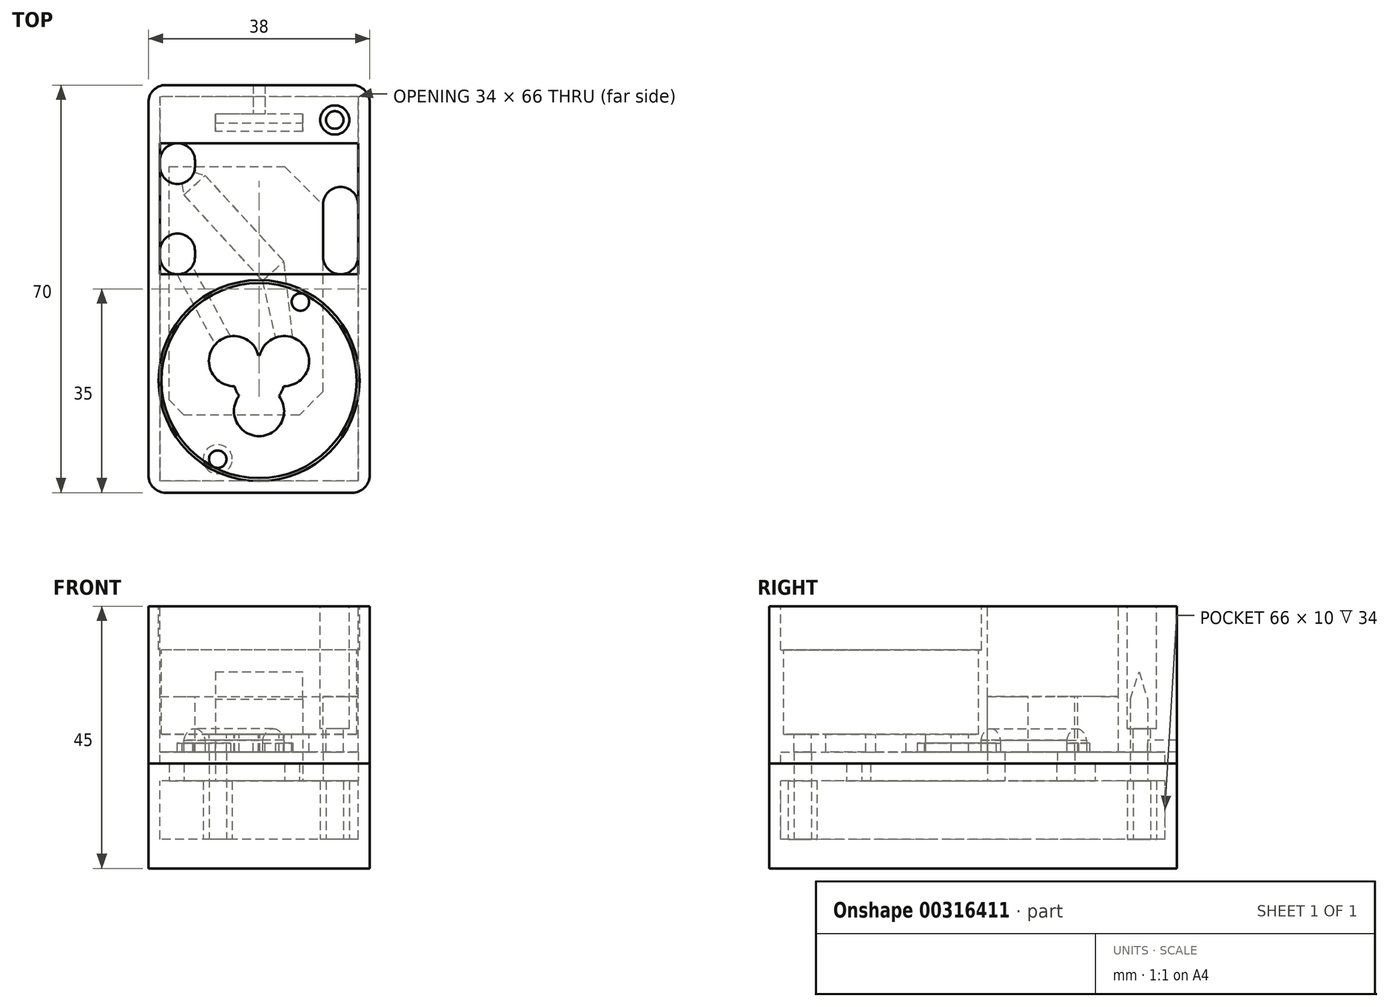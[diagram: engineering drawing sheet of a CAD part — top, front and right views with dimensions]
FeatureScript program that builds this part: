
annotation { "Feature Type Name" : "Feature", "Feature Type Description" : "" }
export const myFeature = defineFeature(function(context is Context, id is Id, definition is map)
    precondition{}
    {
        {
            var Q0;
            Q0=qCreatedBy(makeId("Top.planeOp"),FACE);
            var sketch = newSketch(context, id + "F0", { "sketchPlane" : qUnion([Q0])});
            skLineSegment(sketch, "E0.bottom", {"start": v(-16, 35) * mm, "end": v(16, 35) * mm});
            skLineSegment(sketch, "E0.top", {"start": v(-16, -35) * mm, "end": v(16, -35) * mm});
            skLineSegment(sketch, "E0.left", {"start": v(-19, 32) * mm, "end": v(-19, -32) * mm});
            skLineSegment(sketch, "E0.right", {"start": v(19, 32) * mm, "end": v(19, -32) * mm});
            skPoint(sketch, "E1.visualSharp", {"position": v(-19, 35) * mm});
            skArc(sketch, "E1.filletArc", {"start": v(-16, 35) * mm, "mid": v(-18.12, 34.12) * mm, "end": v(-19, 32) * mm});
            skPoint(sketch, "E2.visualSharp", {"position": v(-19, -35) * mm});
            skArc(sketch, "E2.filletArc", {"start": v(-19, -32) * mm, "mid": v(-18.12, -34.12) * mm, "end": v(-16, -35) * mm});
            skPoint(sketch, "E3.visualSharp", {"position": v(19, -35) * mm});
            skArc(sketch, "E3.filletArc", {"start": v(16, -35) * mm, "mid": v(18.12, -34.12) * mm, "end": v(19, -32) * mm});
            skPoint(sketch, "E4.visualSharp", {"position": v(19, 35) * mm});
            skArc(sketch, "E4.filletArc", {"start": v(19, 32) * mm, "mid": v(18.12, 34.12) * mm, "end": v(16, 35) * mm});
            skSolve(sketch);
        }
        {
            var Q0;
            Q0 = qSketchRegion(id + "F0", true);
            extrude(context, id + "F1", {"entities" : qUnion([Q0]), "depth" : 27 * mm});
        }
        {
            var Q0;
            Q0=makeQuery(id+"F1.opExtrude","CAP_FACE",FACE,{"disambiguationData":[OSD([sQuery(id+"F0.wireOp",EDGE,"E0.bottom"),sQuery(id+"F0.wireOp",EDGE,"E0.top"),sQuery(id+"F0.wireOp",EDGE,"E0.left"),sQuery(id+"F0.wireOp",EDGE,"E0.right"),sQuery(id+"F0.wireOp",EDGE,"E1.filletArc"),sQuery(id+"F0.wireOp",EDGE,"E2.filletArc"),sQuery(id+"F0.wireOp",EDGE,"E3.filletArc"),sQuery(id+"F0.wireOp",EDGE,"E4.filletArc")])],"isStart":false});
            var sketch = newSketch(context, id + "F2", { "sketchPlane" : qUnion([Q0])});
            skCircle(sketch, "E5", {"center": v(13, 29) * mm, "radius": 2.5 * mm});
            skSolve(sketch);
        }
        {
            var Q0;
            Q0 = qSketchRegion(id + "F2", true);
            extrude(context, id + "F3", {"entities" : qUnion([Q0]), "operationType" : NewBodyOperationType.REMOVE, "oppositeDirection" : true, "depth" : 21 * mm});
        }
        {
            var Q0;
            Q0=makeQuery(id+"F3.boolean.opBoolean","COPY",FACE,{"derivedFrom":makeQuery(id+"F3.opExtrude","CAP_FACE",FACE,{"disambiguationData":[OSD([sQuery(id+"F2.wireOp",EDGE,"E5")])],"isStart":false})});
            var sketch = newSketch(context, id + "F4", { "sketchPlane" : qUnion([Q0])});
            skCircle(sketch, "E6", {"center": v(13, 29) * mm, "radius": 1.5 * mm});
            skSolve(sketch);
        }
        {
            var Q0;
            Q0 = qSketchRegion(id + "F4", true);
            extrude(context, id + "F5", {"entities" : qUnion([Q0]), "operationType" : NewBodyOperationType.REMOVE, "oppositeDirection" : true, "depth" : 10 * mm});
        }
        {
            var Q0;
            Q0=makeQuery(id+"F1.opExtrude","CAP_FACE",FACE,{"disambiguationData":[OSD([sQuery(id+"F0.wireOp",EDGE,"E0.bottom"),sQuery(id+"F0.wireOp",EDGE,"E0.top"),sQuery(id+"F0.wireOp",EDGE,"E0.left"),sQuery(id+"F0.wireOp",EDGE,"E0.right"),sQuery(id+"F0.wireOp",EDGE,"E1.filletArc"),sQuery(id+"F0.wireOp",EDGE,"E2.filletArc"),sQuery(id+"F0.wireOp",EDGE,"E3.filletArc"),sQuery(id+"F0.wireOp",EDGE,"E4.filletArc")])],"isStart":false});
            var sketch = newSketch(context, id + "F6", { "sketchPlane" : qUnion([Q0])});
            skCircle(sketch, "E7", {"center": v(0, -15.75) * mm, "radius": 17.25 * mm});
            skSolve(sketch);
        }
        {
            var Q0;
            Q0 = qSketchRegion(id + "F6", true);
            extrude(context, id + "F7", {"entities" : qUnion([Q0]), "operationType" : NewBodyOperationType.REMOVE, "oppositeDirection" : true, "depth" : 7.5 * mm});
        }
        {
            var Q0;
            Q0=makeQuery(id+"F7.boolean.opBoolean","COPY",FACE,{"derivedFrom":makeQuery(id+"F7.opExtrude","CAP_FACE",FACE,{"disambiguationData":[OSD([sQuery(id+"F6.wireOp",EDGE,"E7")])],"isStart":false})});
            var sketch = newSketch(context, id + "F8", { "sketchPlane" : qUnion([Q0])});
            skCircle(sketch, "E8", {"center": v(0, -15.75) * mm, "radius": 16.75 * mm});
            skSolve(sketch);
        }
        {
            var Q0;
            Q0 = qSketchRegion(id + "F8", true);
            var Q1;
            Q1 = qSketchRegion(id + "F10", true);
            extrude(context, id + "F9", {"entities" : qUnion([Q0, Q1]), "operationType" : NewBodyOperationType.REMOVE, "oppositeDirection" : true, "depth" : 14.5 * mm});
        }
        {
            var Q0;
            Q0=makeQuery(id+"F1.opExtrude","CAP_FACE",FACE,{"disambiguationData":[OSD([sQuery(id+"F0.wireOp",EDGE,"E0.bottom"),sQuery(id+"F0.wireOp",EDGE,"E0.top"),sQuery(id+"F0.wireOp",EDGE,"E0.left"),sQuery(id+"F0.wireOp",EDGE,"E0.right"),sQuery(id+"F0.wireOp",EDGE,"E1.filletArc"),sQuery(id+"F0.wireOp",EDGE,"E2.filletArc"),sQuery(id+"F0.wireOp",EDGE,"E3.filletArc"),sQuery(id+"F0.wireOp",EDGE,"E4.filletArc")])],"isStart":false});
            var sketch = newSketch(context, id + "F10", { "sketchPlane" : qUnion([Q0])});
            skLineSegment(sketch, "E9.bottom", {"start": v(-17, 25) * mm, "end": v(17, 25) * mm});
            skLineSegment(sketch, "E9.top", {"start": v(-17, 2.5) * mm, "end": v(17, 2.5) * mm});
            skLineSegment(sketch, "E9.left", {"start": v(-17, 25) * mm, "end": v(-17, 2.5) * mm});
            skLineSegment(sketch, "E9.right", {"start": v(17, 25) * mm, "end": v(17, 2.5) * mm});
            skSolve(sketch);
        }
        {
            var Q0;
            Q0 = qSketchRegion(id + "F10", true);
            extrude(context, id + "F11", {"entities" : qUnion([Q0]), "operationType" : NewBodyOperationType.REMOVE, "oppositeDirection" : true, "depth" : 15.5 * mm});
        }
        {
            var Q0;
            Q0=makeQuery(id+"F1.opExtrude","CAP_FACE",FACE,{"disambiguationData":[OSD([sQuery(id+"F0.wireOp",EDGE,"E0.bottom"),sQuery(id+"F0.wireOp",EDGE,"E0.top"),sQuery(id+"F0.wireOp",EDGE,"E0.left"),sQuery(id+"F0.wireOp",EDGE,"E0.right"),sQuery(id+"F0.wireOp",EDGE,"E1.filletArc"),sQuery(id+"F0.wireOp",EDGE,"E2.filletArc"),sQuery(id+"F0.wireOp",EDGE,"E3.filletArc"),sQuery(id+"F0.wireOp",EDGE,"E4.filletArc")])],"isStart":true});
            var sketch = newSketch(context, id + "F12", { "sketchPlane" : qUnion([Q0])});
            skLineSegment(sketch, "E10.bottom", {"start": v(17, -33) * mm, "end": v(-17, -33) * mm});
            skLineSegment(sketch, "E10.top", {"start": v(17, 33) * mm, "end": v(-17, 33) * mm});
            skLineSegment(sketch, "E10.left", {"start": v(17, -33) * mm, "end": v(17, 33) * mm});
            skLineSegment(sketch, "E10.right", {"start": v(-17, -33) * mm, "end": v(-17, 33) * mm});
            skSolve(sketch);
        }
        {
            var Q0;
            Q0 = qSketchRegion(id + "F12", true);
            extrude(context, id + "F13", {"entities" : qUnion([Q0]), "operationType" : NewBodyOperationType.REMOVE, "oppositeDirection" : true, "depth" : 2 * mm});
        }
        {
            var Q0;
            Q0=makeQuery(id+"F9.boolean.opBoolean","COPY",FACE,{"derivedFrom":makeQuery(id+"F9.opExtrude","CAP_FACE",FACE,{"disambiguationData":[OSD([sQuery(id+"F8.wireOp",EDGE,"E8")])],"isStart":false})});
            var sketch = newSketch(context, id + "F14", { "sketchPlane" : qUnion([Q0])});
            skCircle(sketch, "E11", {"center": v(-4.3, -12.4) * mm, "radius": 4.3 * mm});
            skCircle(sketch, "E12", {"center": v(4.3, -12.4) * mm, "radius": 4.3 * mm});
            skCircle(sketch, "E13", {"center": v(0, -20.98) * mm, "radius": 4.3 * mm});
            skCircle(sketch, "E14", {"center": v(0, -15.75) * mm, "radius": 4.3 * mm});
            skCircle(sketch, "E15", {"center": v(7.1, -2.25) * mm, "radius": 1.5 * mm});
            skCircle(sketch, "E16", {"center": v(-7.1, -29.25) * mm, "radius": 1.5 * mm});
            skSolve(sketch);
        }
        {
            var Q0;
            Q0 = qSketchRegion(id + "F14", true);
            extrude(context, id + "F15", {"entities" : qUnion([Q0]), "operationType" : NewBodyOperationType.REMOVE, "endBound" : BoundingType.UP_TO_NEXT, "oppositeDirection" : true, "depth" : 25 * mm});
        }
        {
            var Q0;
            Q0=makeQuery(id+"F11.boolean.opBoolean","COPY",FACE,{"derivedFrom":makeQuery(id+"F11.opExtrude","CAP_FACE",FACE,{"disambiguationData":[OSD([sQuery(id+"F10.wireOp",EDGE,"E9.bottom"),sQuery(id+"F10.wireOp",EDGE,"E9.top"),sQuery(id+"F10.wireOp",EDGE,"E9.left"),sQuery(id+"F10.wireOp",EDGE,"E9.right")])],"isStart":false})});
            var sketch = newSketch(context, id + "F16", { "sketchPlane" : qUnion([Q0])});
            skLineSegment(sketch, "E17.bottom", {"start": v(-14, 2.5) * mm, "end": v(-14, 2.5) * mm});
            skLineSegment(sketch, "E17.top", {"start": v(-14, 9.5) * mm, "end": v(-14, 9.5) * mm});
            skLineSegment(sketch, "E17.left", {"start": v(-17, 5.5) * mm, "end": v(-17, 6.5) * mm});
            skLineSegment(sketch, "E17.right", {"start": v(-11, 5.5) * mm, "end": v(-11, 6.5) * mm});
            skLineSegment(sketch, "E18.bottom", {"start": v(-14, 25) * mm, "end": v(-14, 25) * mm});
            skLineSegment(sketch, "E18.top", {"start": v(-14, 18) * mm, "end": v(-14, 18) * mm});
            skLineSegment(sketch, "E18.left", {"start": v(-17, 22) * mm, "end": v(-17, 21) * mm});
            skLineSegment(sketch, "E18.right", {"start": v(-11, 22) * mm, "end": v(-11, 21) * mm});
            skPoint(sketch, "E19.visualSharp", {"position": v(-11, 18) * mm});
            skArc(sketch, "E19.filletArc", {"start": v(-14, 18) * mm, "mid": v(-11.88, 18.88) * mm, "end": v(-11, 21) * mm});
            skPoint(sketch, "E20.visualSharp", {"position": v(-11, 9.5) * mm});
            skArc(sketch, "E20.filletArc", {"start": v(-11, 6.5) * mm, "mid": v(-11.88, 8.62) * mm, "end": v(-14, 9.5) * mm});
            skLineSegment(sketch, "E21.bottom", {"start": v(14, 2.5) * mm, "end": v(14, 2.5) * mm});
            skLineSegment(sketch, "E21.top", {"start": v(14, 17.5) * mm, "end": v(14, 17.5) * mm});
            skLineSegment(sketch, "E21.left", {"start": v(17, 5.5) * mm, "end": v(17, 14.5) * mm});
            skLineSegment(sketch, "E21.right", {"start": v(11, 5.5) * mm, "end": v(11, 14.5) * mm});
            skPoint(sketch, "E22.visualSharp", {"position": v(-17, 18) * mm});
            skArc(sketch, "E22.filletArc", {"start": v(-17, 21) * mm, "mid": v(-16.12, 18.88) * mm, "end": v(-14, 18) * mm});
            skPoint(sketch, "E23.visualSharp", {"position": v(-17, 9.5) * mm});
            skArc(sketch, "E23.filletArc", {"start": v(-14, 9.5) * mm, "mid": v(-16.12, 8.62) * mm, "end": v(-17, 6.5) * mm});
            skPoint(sketch, "E24.visualSharp", {"position": v(11, 17.5) * mm});
            skArc(sketch, "E24.filletArc", {"start": v(14, 17.5) * mm, "mid": v(11.88, 16.62) * mm, "end": v(11, 14.5) * mm});
            skPoint(sketch, "E25.visualSharp", {"position": v(17, 17.5) * mm});
            skArc(sketch, "E25.filletArc", {"start": v(17, 14.5) * mm, "mid": v(16.12, 16.62) * mm, "end": v(14, 17.5) * mm});
            skPoint(sketch, "E26.visualSharp", {"position": v(11, 2.5) * mm});
            skArc(sketch, "E26.filletArc", {"start": v(11, 5.5) * mm, "mid": v(11.88, 3.38) * mm, "end": v(14, 2.5) * mm});
            skPoint(sketch, "E27.visualSharp", {"position": v(17, 2.5) * mm});
            skArc(sketch, "E27.filletArc", {"start": v(14, 2.5) * mm, "mid": v(16.12, 3.38) * mm, "end": v(17, 5.5) * mm});
            skPoint(sketch, "E28.visualSharp", {"position": v(-11, 25) * mm});
            skArc(sketch, "E28.filletArc", {"start": v(-11, 22) * mm, "mid": v(-11.88, 24.12) * mm, "end": v(-14, 25) * mm});
            skPoint(sketch, "E29.visualSharp", {"position": v(-17, 25) * mm});
            skArc(sketch, "E29.filletArc", {"start": v(-14, 25) * mm, "mid": v(-16.12, 24.12) * mm, "end": v(-17, 22) * mm});
            skPoint(sketch, "E30.visualSharp", {"position": v(-17, 2.5) * mm});
            skArc(sketch, "E30.filletArc", {"start": v(-17, 5.5) * mm, "mid": v(-16.12, 3.38) * mm, "end": v(-14, 2.5) * mm});
            skPoint(sketch, "E31.visualSharp", {"position": v(-11, 2.5) * mm});
            skArc(sketch, "E31.filletArc", {"start": v(-14, 2.5) * mm, "mid": v(-11.88, 3.38) * mm, "end": v(-11, 5.5) * mm});
            skSolve(sketch);
        }
        {
            var Q0;
            Q0 = qSketchRegion(id + "F16", true);
            extrude(context, id + "F17", {"entities" : qUnion([Q0]), "operationType" : NewBodyOperationType.REMOVE, "endBound" : BoundingType.UP_TO_NEXT, "oppositeDirection" : true, "depth" : 25 * mm});
        }
        {
            var Q0;
            Q0=makeQuery(id+"F13.boolean.opBoolean","COPY",FACE,{"derivedFrom":makeQuery(id+"F13.opExtrude","CAP_FACE",FACE,{"disambiguationData":[OSD([sQuery(id+"F12.wireOp",EDGE,"E10.bottom"),sQuery(id+"F12.wireOp",EDGE,"E10.top"),sQuery(id+"F12.wireOp",EDGE,"E10.left"),sQuery(id+"F12.wireOp",EDGE,"E10.right")])],"isStart":false})});
            var sketch = newSketch(context, id + "F18", { "sketchPlane" : qUnion([Q0])});
            skLineSegment(sketch, "E32", {"start": v(-12.92, -16.12) * mm, "end": v(-9.23, -19.5) * mm});
            skLineSegment(sketch, "E33", {"start": v(-9.23, -19.5) * mm, "end": v(4.27, -4.74) * mm});
            skLineSegment(sketch, "E34", {"start": v(4.27, -4.74) * mm, "end": v(0.58, -1.36) * mm});
            skLineSegment(sketch, "E35", {"start": v(0.58, -1.36) * mm, "end": v(-12.92, -16.12) * mm});
            skLineSegment(sketch, "E36", {"start": v(0.58, -1.36) * mm, "end": v(2.8, 8.37) * mm});
            skLineSegment(sketch, "E37", {"start": v(2.8, 8.37) * mm, "end": v(5.8, 8.37) * mm});
            skLineSegment(sketch, "E38", {"start": v(5.8, 8.37) * mm, "end": v(4.27, -4.74) * mm});
            skPoint(sketch, "E39", {"position": v(-11.08, -17.8) * mm});
            skLineSegment(sketch, "E40", {"start": v(-11.16, -20.02) * mm, "end": v(-13.28, -18.09) * mm});
            skLineSegment(sketch, "E41", {"start": v(-13.28, -18.09) * mm, "end": v(-12.92, -16.12) * mm});
            skLineSegment(sketch, "E42", {"start": v(-11.16, -20.02) * mm, "end": v(-9.23, -19.5) * mm});
            skSolve(sketch);
        }
        {
            var Q0;
            Q0 = qSketchRegion(id + "F18", true);
            extrude(context, id + "F19", {"entities" : qUnion([Q0]), "operationType" : NewBodyOperationType.REMOVE, "oppositeDirection" : true, "depth" : 1.5 * mm});
        }
        {
            var Q0;
            Q0=makeQuery(id+"F13.boolean.opBoolean","COPY",FACE,{"derivedFrom":makeQuery(id+"F13.opExtrude","CAP_FACE",FACE,{"disambiguationData":[OSD([sQuery(id+"F12.wireOp",EDGE,"E10.bottom"),sQuery(id+"F12.wireOp",EDGE,"E10.top"),sQuery(id+"F12.wireOp",EDGE,"E10.left"),sQuery(id+"F12.wireOp",EDGE,"E10.right")])],"isStart":false})});
            var sketch = newSketch(context, id + "F20", { "sketchPlane" : qUnion([Q0])});
            skLineSegment(sketch, "E43", {"start": v(-14.08, -2.5) * mm, "end": v(-7.54, 9.57) * mm});
            skLineSegment(sketch, "E44", {"start": v(-7.54, 9.57) * mm, "end": v(-4.9, 8.14) * mm});
            skLineSegment(sketch, "E45", {"start": v(-4.9, 8.14) * mm, "end": v(-11.44, -3.93) * mm});
            skLineSegment(sketch, "E46", {"start": v(-11.44, -3.93) * mm, "end": v(-14.08, -2.5) * mm});
            skSolve(sketch);
        }
        {
            var Q0;
            Q0=makeQuery(id+"F19.boolean.opBoolean","COPY",VERTEX,{"derivedFrom":makeQuery(id+"F19.opExtrude","CAP_VERTEX",VERTEX,{"disambiguationData":[OSD([sQuery(id+"F18.wireOp",EDGE,"E32"),sQuery(id+"F18.wireOp",EDGE,"E35"),sQuery(id+"F18.wireOp",EDGE,"E41")])],"isStart":true})});
            var Q1;
            Q1=makeQuery(id+"F19.boolean.opBoolean","COPY",VERTEX,{"derivedFrom":makeQuery(id+"F19.opExtrude","CAP_VERTEX",VERTEX,{"disambiguationData":[OSD([sQuery(id+"F18.wireOp",EDGE,"E32"),sQuery(id+"F18.wireOp",EDGE,"E33"),sQuery(id+"F18.wireOp",EDGE,"E42")])],"isStart":true})});
            var Q2;
            Q2=makeQuery(id+"F19.boolean.opBoolean","COPY",VERTEX,{"derivedFrom":makeQuery(id+"F19.opExtrude","CAP_VERTEX",VERTEX,{"disambiguationData":[OSD([sQuery(id+"F18.wireOp",EDGE,"E32"),sQuery(id+"F18.wireOp",EDGE,"E33"),sQuery(id+"F18.wireOp",EDGE,"E42")])],"isStart":false})});
            cPlane(context, id + "F21", {"entities" : qUnion([Q0, Q1, Q2]), "cplaneType" : CPlaneType.THREE_POINT, "offset" : 25 * mm, "width" : 150 * mm, "height" : 150 * mm});
        }
        {
            var Q0;
            Q0=qCreatedBy(id+"F21.planeOp",FACE);
            var sketch = newSketch(context, id + "F22", { "sketchPlane" : qUnion([Q0])});
            skCircle(sketch, "E47", {"center": v(-3.85, 3.5) * mm, "radius": 2.5 * mm});
            skSolve(sketch);
        }
        {
            var Q0;
            Q0 = qSketchRegion(id + "F22", true);
            extrude(context, id + "F23", {"entities" : qUnion([Q0]), "operationType" : NewBodyOperationType.REMOVE, "oppositeDirection" : true, "depth" : 20 * mm});
        }
        {
            var Q0;
            Q0 = qSketchRegion(id + "F20", true);
            extrude(context, id + "F24", {"entities" : qUnion([Q0]), "operationType" : NewBodyOperationType.REMOVE, "oppositeDirection" : true, "depth" : 1.5 * mm});
        }
        {
            var Q0;
            {var subQ3=sQuery(id+"F12.wireOp",EDGE,"E10.top");var subQ4=sQuery(id+"F12.wireOp",EDGE,"E10.bottom");var subQ6=sQuery(id+"F12.wireOp",EDGE,"E10.left");var subQ7=sQuery(id+"F12.wireOp",EDGE,"E10.right");Q0=makeQuery(id+"F24.boolean.opBoolean","SPLIT",FACE,{"disambiguationData":[TD([makeQuery(id+"F11.boolean.opBoolean","COPY",FACE,{"derivedFrom":makeQuery(id+"F11.opExtrude","SWEPT_FACE",FACE,{"disambiguationData":[OSD([sQuery(id+"F10.wireOp",EDGE,"E9.right")])]})})])],"derivedFrom":makeQuery(id+"F13.boolean.opBoolean","COPY",FACE,{"derivedFrom":makeQuery(id+"F13.opExtrude","CAP_FACE",FACE,{"disambiguationData":[OSD([subQ4,subQ3,subQ6,subQ7])],"isStart":false})})});}
            var sketch = newSketch(context, id + "F25", { "sketchPlane" : qUnion([Q0])});
            skLineSegment(sketch, "E48.bottom", {"start": v(7.5, -30) * mm, "end": v(-7.5, -30) * mm});
            skLineSegment(sketch, "E48.top", {"start": v(7.5, -27) * mm, "end": v(-7.5, -27) * mm});
            skLineSegment(sketch, "E48.left", {"start": v(7.5, -30) * mm, "end": v(7.5, -27) * mm});
            skLineSegment(sketch, "E48.right", {"start": v(-7.5, -30) * mm, "end": v(-7.5, -27) * mm});
            skSolve(sketch);
        }
        {
            var Q0;
            Q0 = qSketchRegion(id + "F25", true);
            extrude(context, id + "F26", {"entities" : qUnion([Q0]), "operationType" : NewBodyOperationType.REMOVE, "oppositeDirection" : true, "depth" : 9 * mm});
        }
        {
            var Q0;
            Q0=makeQuery(id+"F26.boolean.opBoolean","COPY",FACE,{"derivedFrom":makeQuery(id+"F26.opExtrude","SWEPT_FACE",FACE,{"disambiguationData":[OSD([sQuery(id+"F25.wireOp",EDGE,"E48.bottom")])]})});
            var sketch = newSketch(context, id + "F27", { "sketchPlane" : qUnion([Q0])});
            skLineSegment(sketch, "E49.bottom", {"start": v(1, 2) * mm, "end": v(-1, 2) * mm});
            skLineSegment(sketch, "E49.top", {"start": v(1, 4) * mm, "end": v(-1, 4) * mm});
            skLineSegment(sketch, "E49.left", {"start": v(1, 2) * mm, "end": v(1, 4) * mm});
            skLineSegment(sketch, "E49.right", {"start": v(-1, 2) * mm, "end": v(-1, 4) * mm});
            skSolve(sketch);
        }
        {
            var Q0;
            Q0 = qSketchRegion(id + "F27", true);
            extrude(context, id + "F28", {"entities" : qUnion([Q0]), "operationType" : NewBodyOperationType.REMOVE, "endBound" : BoundingType.UP_TO_NEXT, "oppositeDirection" : true, "depth" : 25 * mm});
        }
        {
            var Q0;
            Q0=makeQuery(id+"F26.boolean.opBoolean","COPY",FACE,{"derivedFrom":makeQuery(id+"F26.opExtrude","SWEPT_FACE",FACE,{"disambiguationData":[OSD([sQuery(id+"F25.wireOp",EDGE,"E48.left")])]})});
            var sketch = newSketch(context, id + "F29", { "sketchPlane" : qUnion([Q0])});
            skLineSegment(sketch, "E50", {"start": v(-27, 11) * mm, "end": v(-28.5, 15.77) * mm});
            skLineSegment(sketch, "E51", {"start": v(-28.5, 15.77) * mm, "end": v(-30, 11) * mm});
            skLineSegment(sketch, "E52", {"start": v(-30, 11) * mm, "end": v(-27, 11) * mm});
            skSolve(sketch);
        }
        {
            var Q0;
            Q0 = qSketchRegion(id + "F29", true);
            extrude(context, id + "F30", {"entities" : qUnion([Q0]), "operationType" : NewBodyOperationType.REMOVE, "depth" : 15 * mm});
        }
        {
            var Q0;
            Q0=qCreatedBy(makeId("Top.planeOp"),FACE);
            var sketch = newSketch(context, id + "F31", { "sketchPlane" : qUnion([Q0])});
            skLineSegment(sketch, "E53.bottom", {"start": v(-17, -33) * mm, "end": v(17, -33) * mm});
            skLineSegment(sketch, "E53.top", {"start": v(-17, 33) * mm, "end": v(17, 33) * mm});
            skLineSegment(sketch, "E53.left", {"start": v(-17, -33) * mm, "end": v(-17, 33) * mm});
            skLineSegment(sketch, "E53.right", {"start": v(17, -33) * mm, "end": v(17, 33) * mm});
            skSolve(sketch);
        }
        {
            var Q0;
            Q0 = qSketchRegion(id + "F31", true);
            extrude(context, id + "F32", {"entities" : qUnion([Q0]), "operationType" : NewBodyOperationType.ADD, "oppositeDirection" : true, "depth" : 5 * mm});
        }
        {
            var Q0;
            Q0=makeQuery(id+"F19.boolean.opBoolean","COPY",FACE,{"derivedFrom":makeQuery(id+"F19.opExtrude","CAP_FACE",FACE,{"disambiguationData":[OSD([sQuery(id+"F18.wireOp",EDGE,"E33"),sQuery(id+"F18.wireOp",EDGE,"E35"),sQuery(id+"F18.wireOp",EDGE,"E36"),sQuery(id+"F18.wireOp",EDGE,"E37"),sQuery(id+"F18.wireOp",EDGE,"E38"),sQuery(id+"F18.wireOp",EDGE,"E40"),sQuery(id+"F18.wireOp",EDGE,"E41"),sQuery(id+"F18.wireOp",EDGE,"E42")])],"isStart":false})});
            var sketch = newSketch(context, id + "F33", { "sketchPlane" : qUnion([Q0])});
            skLineSegment(sketch, "E54", {"start": v(4.27, -4.74) * mm, "end": v(-9.23, -19.5) * mm});
            skLineSegment(sketch, "E55", {"start": v(-9.23, -19.5) * mm, "end": v(-12.92, -16.12) * mm});
            skLineSegment(sketch, "E56", {"start": v(-12.92, -16.12) * mm, "end": v(0.58, -1.36) * mm});
            skLineSegment(sketch, "E57", {"start": v(0.58, -1.36) * mm, "end": v(4.27, -4.74) * mm});
            skSolve(sketch);
        }
        {
            var Q0;
            Q0 = qSketchRegion(id + "F33", true);
            extrude(context, id + "F34", {"entities" : qUnion([Q0]), "operationType" : NewBodyOperationType.REMOVE, "oppositeDirection" : true, "depth" : 0.5 * mm});
        }
        {
            var Q0;
            Q0=makeQuery(id+"F32.opExtrude","CAP_FACE",FACE,{"disambiguationData":[OSD([sQuery(id+"F31.wireOp",EDGE,"E53.bottom"),sQuery(id+"F31.wireOp",EDGE,"E53.top"),sQuery(id+"F31.wireOp",EDGE,"E53.left"),sQuery(id+"F31.wireOp",EDGE,"E53.right")])],"isStart":false});
            var sketch = newSketch(context, id + "F35", { "sketchPlane" : qUnion([Q0])});
            skLineSegment(sketch, "E58.bottom", {"start": v(-16, 35) * mm, "end": v(16, 35) * mm});
            skLineSegment(sketch, "E58.top", {"start": v(-16, -35) * mm, "end": v(16, -35) * mm});
            skLineSegment(sketch, "E58.left", {"start": v(-19, 32) * mm, "end": v(-19, -32) * mm});
            skLineSegment(sketch, "E58.right", {"start": v(19, 32) * mm, "end": v(19, -32) * mm});
            skPoint(sketch, "E59.visualSharp", {"position": v(-19, 35) * mm});
            skArc(sketch, "E59.filletArc", {"start": v(-16, 35) * mm, "mid": v(-18.12, 34.12) * mm, "end": v(-19, 32) * mm});
            skPoint(sketch, "E60.visualSharp", {"position": v(19, 35) * mm});
            skArc(sketch, "E60.filletArc", {"start": v(19, 32) * mm, "mid": v(18.12, 34.12) * mm, "end": v(16, 35) * mm});
            skPoint(sketch, "E61.visualSharp", {"position": v(19, -35) * mm});
            skArc(sketch, "E61.filletArc", {"start": v(16, -35) * mm, "mid": v(18.12, -34.12) * mm, "end": v(19, -32) * mm});
            skPoint(sketch, "E62.visualSharp", {"position": v(-19, -35) * mm});
            skArc(sketch, "E62.filletArc", {"start": v(-19, -32) * mm, "mid": v(-18.12, -34.12) * mm, "end": v(-16, -35) * mm});
            skSolve(sketch);
        }
        {
            var Q0;
            Q0 = qSketchRegion(id + "F35", true);
            extrude(context, id + "F36", {"entities" : qUnion([Q0]), "operationType" : NewBodyOperationType.ADD, "oppositeDirection" : true, "depth" : 3 * mm});
        }
        {
            var Q0;
            Q0=makeQuery(id+"F36.boolean.opBoolean","MERGE",FACE,{"derivedFrom":[makeQuery(id+"F32.opExtrude","CAP_FACE",FACE,{"disambiguationData":[OSD([sQuery(id+"F31.wireOp",EDGE,"E53.bottom"),sQuery(id+"F31.wireOp",EDGE,"E53.top"),sQuery(id+"F31.wireOp",EDGE,"E53.left"),sQuery(id+"F31.wireOp",EDGE,"E53.right")])],"isStart":false}),makeQuery(id+"F36.opExtrude","CAP_FACE",FACE,{"disambiguationData":[OSD([sQuery(id+"F35.wireOp",EDGE,"E58.bottom"),sQuery(id+"F35.wireOp",EDGE,"E58.top"),sQuery(id+"F35.wireOp",EDGE,"E58.left"),sQuery(id+"F35.wireOp",EDGE,"E58.right"),sQuery(id+"F35.wireOp",EDGE,"E59.filletArc"),sQuery(id+"F35.wireOp",EDGE,"E60.filletArc"),sQuery(id+"F35.wireOp",EDGE,"E61.filletArc"),sQuery(id+"F35.wireOp",EDGE,"E62.filletArc")])],"isStart":true})]});
            var sketch = newSketch(context, id + "F37", { "sketchPlane" : qUnion([Q0])});
            skArc(sketch, "E63.0", {"start": v(17, -14.5) * mm, "mid": v(14, -17.5) * mm, "end": v(11, -14.5) * mm});
            skLineSegment(sketch, "E63.1", {"start": v(11, -5.5) * mm, "end": v(11, -14.5) * mm});
            skArc(sketch, "E63.2", {"start": v(11, -5.5) * mm, "mid": v(11.88, -3.38) * mm, "end": v(14, -2.5) * mm});
            skArc(sketch, "E63.3", {"start": v(14, -2.5) * mm, "mid": v(16.12, -3.38) * mm, "end": v(17, -5.5) * mm});
            skLineSegment(sketch, "E64", {"start": v(17, -14.5) * mm, "end": v(17, -5.5) * mm});
            skCircle(sketch, "E65.1", {"center": v(-7.1, 29.25) * mm, "radius": 1.5 * mm});
            skLineSegment(sketch, "E66.0", {"start": v(7.5, -27) * mm, "end": v(-7.5, -27) * mm});
            skLineSegment(sketch, "E66.1", {"start": v(7.5, -30) * mm, "end": v(7.5, -27) * mm});
            skLineSegment(sketch, "E66.2", {"start": v(-7.5, -30) * mm, "end": v(-7.5, -27) * mm});
            skLineSegment(sketch, "E66.3", {"start": v(7.5, -30) * mm, "end": v(-7.5, -30) * mm});
            skSolve(sketch);
        }
        {
            var Q0;
            Q0 = qSketchRegion(id + "F37", true);
            extrude(context, id + "F38", {"entities" : qUnion([Q0]), "operationType" : NewBodyOperationType.REMOVE, "endBound" : BoundingType.UP_TO_NEXT, "oppositeDirection" : true, "depth" : 25 * mm});
        }
        {
            var Q0;
            Q0=makeQuery(id+"F36.boolean.opBoolean","MERGE",FACE,{"derivedFrom":[makeQuery(id+"F32.opExtrude","CAP_FACE",FACE,{"disambiguationData":[OSD([sQuery(id+"F31.wireOp",EDGE,"E53.bottom"),sQuery(id+"F31.wireOp",EDGE,"E53.top"),sQuery(id+"F31.wireOp",EDGE,"E53.left"),sQuery(id+"F31.wireOp",EDGE,"E53.right")])],"isStart":false}),makeQuery(id+"F36.opExtrude","CAP_FACE",FACE,{"disambiguationData":[OSD([sQuery(id+"F35.wireOp",EDGE,"E58.bottom"),sQuery(id+"F35.wireOp",EDGE,"E58.top"),sQuery(id+"F35.wireOp",EDGE,"E58.left"),sQuery(id+"F35.wireOp",EDGE,"E58.right"),sQuery(id+"F35.wireOp",EDGE,"E59.filletArc"),sQuery(id+"F35.wireOp",EDGE,"E60.filletArc"),sQuery(id+"F35.wireOp",EDGE,"E61.filletArc"),sQuery(id+"F35.wireOp",EDGE,"E62.filletArc")])],"isStart":true})]});
            var sketch = newSketch(context, id + "F39", { "sketchPlane" : qUnion([Q0])});
            skLineSegment(sketch, "E67", {"start": v(-15.4, -21) * mm, "end": v(4.4, -21) * mm});
            skLineSegment(sketch, "E68", {"start": v(4.4, -21) * mm, "end": v(11, -14.4) * mm});
            skLineSegment(sketch, "E69", {"start": v(11, -14.4) * mm, "end": v(11, 17.6) * mm});
            skLineSegment(sketch, "E70", {"start": v(11, 17.6) * mm, "end": v(6.9, 21.7) * mm});
            skLineSegment(sketch, "E71", {"start": v(6.9, 21.7) * mm, "end": v(-12.9, 21.7) * mm});
            skLineSegment(sketch, "E72", {"start": v(-12.9, 21.7) * mm, "end": v(-15.4, 19.1) * mm});
            skLineSegment(sketch, "E73", {"start": v(-15.4, 19.1) * mm, "end": v(-15.4, -21) * mm});
            skSolve(sketch);
        }
        {
            var Q0;
            Q0 = qSketchRegion(id + "F39", true);
            extrude(context, id + "F40", {"entities" : qUnion([Q0]), "operationType" : NewBodyOperationType.REMOVE, "oppositeDirection" : true, "depth" : 3 * mm});
        }
        {
            var Q0;
            Q0=makeQuery(id+"F36.boolean.opBoolean","MERGE",FACE,{"derivedFrom":[makeQuery(id+"F32.opExtrude","CAP_FACE",FACE,{"disambiguationData":[OSD([sQuery(id+"F31.wireOp",EDGE,"E53.bottom"),sQuery(id+"F31.wireOp",EDGE,"E53.top"),sQuery(id+"F31.wireOp",EDGE,"E53.left"),sQuery(id+"F31.wireOp",EDGE,"E53.right")])],"isStart":false}),makeQuery(id+"F36.opExtrude","CAP_FACE",FACE,{"disambiguationData":[OSD([sQuery(id+"F35.wireOp",EDGE,"E58.bottom"),sQuery(id+"F35.wireOp",EDGE,"E58.top"),sQuery(id+"F35.wireOp",EDGE,"E58.left"),sQuery(id+"F35.wireOp",EDGE,"E58.right"),sQuery(id+"F35.wireOp",EDGE,"E59.filletArc"),sQuery(id+"F35.wireOp",EDGE,"E60.filletArc"),sQuery(id+"F35.wireOp",EDGE,"E61.filletArc"),sQuery(id+"F35.wireOp",EDGE,"E62.filletArc")])],"isStart":true})]});
            var sketch = newSketch(context, id + "F41", { "sketchPlane" : qUnion([Q0])});
            skArc(sketch, "E74.0", {"start": v(19, 32) * mm, "mid": v(18.12, 34.12) * mm, "end": v(16, 35) * mm});
            skLineSegment(sketch, "E74.1", {"start": v(-16, 35) * mm, "end": v(16, 35) * mm});
            skArc(sketch, "E74.2", {"start": v(-16, 35) * mm, "mid": v(-18.12, 34.12) * mm, "end": v(-19, 32) * mm});
            skLineSegment(sketch, "E74.3", {"start": v(-19, 32) * mm, "end": v(-19, -32) * mm});
            skArc(sketch, "E74.4", {"start": v(-19, -32) * mm, "mid": v(-18.12, -34.12) * mm, "end": v(-16, -35) * mm});
            skLineSegment(sketch, "E74.5", {"start": v(-16, -35) * mm, "end": v(16, -35) * mm});
            skArc(sketch, "E74.6", {"start": v(16, -35) * mm, "mid": v(18.12, -34.12) * mm, "end": v(19, -32) * mm});
            skLineSegment(sketch, "E74.7", {"start": v(19, 32) * mm, "end": v(19, -32) * mm});
            skLineSegment(sketch, "E75.0", {"start": v(-17, -33) * mm, "end": v(-17, 33) * mm});
            skLineSegment(sketch, "E75.1", {"start": v(17, 33) * mm, "end": v(-17, 33) * mm});
            skLineSegment(sketch, "E75.2", {"start": v(17, -33) * mm, "end": v(17, 33) * mm});
            skLineSegment(sketch, "E75.3", {"start": v(17, -33) * mm, "end": v(-17, -33) * mm});
            skSolve(sketch);
        }
        {
            var Q0;
            Q0 = qSketchRegion(id + "F41", true);
            extrude(context, id + "F42", {"entities" : qUnion([Q0]), "operationType" : NewBodyOperationType.ADD, "depth" : 12 * mm});
        }
        {
            var Q0;
            Q0=makeQuery(id+"F32.opExtrude","SWEPT_BODY",BODY,{"disambiguationData":[OSD([sQuery(id+"F31.wireOp",EDGE,"E53.bottom"),sQuery(id+"F31.wireOp",EDGE,"E53.top"),sQuery(id+"F31.wireOp",EDGE,"E53.left"),sQuery(id+"F31.wireOp",EDGE,"E53.right")])]});
            var Q1;
            Q1=makeQuery(id+"F32.opExtrude","SWEPT_EDGE",EDGE,{"disambiguationData":[OSD([sQuery(id+"F31.wireOp",EDGE,"E53.top"),sQuery(id+"F31.wireOp",EDGE,"E53.right")])]});
            transform(context, id + "F43", {"entities" : qUnion([Q0]), "transformType" : TransformType.TRANSLATION_ENTITY, "oppositeDirectionEntity" : false, "transformLine" : qUnion([Q1]), "makeCopy" : false});
        }
        {
            var Q0;
            Q0=makeQuery(id+"F42.opExtrude","CAP_FACE",FACE,{"disambiguationData":[OSD([sQuery(id+"F41.wireOp",EDGE,"E74.0"),sQuery(id+"F41.wireOp",EDGE,"E74.1"),sQuery(id+"F41.wireOp",EDGE,"E74.2"),sQuery(id+"F41.wireOp",EDGE,"E74.3"),sQuery(id+"F41.wireOp",EDGE,"E74.4"),sQuery(id+"F41.wireOp",EDGE,"E74.5"),sQuery(id+"F41.wireOp",EDGE,"E74.6"),sQuery(id+"F41.wireOp",EDGE,"E74.7"),sQuery(id+"F41.wireOp",EDGE,"E75.0"),sQuery(id+"F41.wireOp",EDGE,"E75.1"),sQuery(id+"F41.wireOp",EDGE,"E75.2"),sQuery(id+"F41.wireOp",EDGE,"E75.3")])],"isStart":false});
            var sketch = newSketch(context, id + "F44", { "sketchPlane" : qUnion([Q0])});
            skArc(sketch, "E76.0", {"start": v(-16, 35) * mm, "mid": v(-18.12, 34.12) * mm, "end": v(-19, 32) * mm});
            skLineSegment(sketch, "E76.1", {"start": v(-19, 32) * mm, "end": v(-19, -32) * mm});
            skLineSegment(sketch, "E76.2", {"start": v(-16, 35) * mm, "end": v(16, 35) * mm});
            skArc(sketch, "E76.3", {"start": v(19, 32) * mm, "mid": v(18.12, 34.12) * mm, "end": v(16, 35) * mm});
            skLineSegment(sketch, "E76.4", {"start": v(19, 32) * mm, "end": v(19, -32) * mm});
            skArc(sketch, "E76.5", {"start": v(16, -35) * mm, "mid": v(18.12, -34.12) * mm, "end": v(19, -32) * mm});
            skLineSegment(sketch, "E76.6", {"start": v(-16, -35) * mm, "end": v(16, -35) * mm});
            skArc(sketch, "E76.7", {"start": v(-19, -32) * mm, "mid": v(-18.12, -34.12) * mm, "end": v(-16, -35) * mm});
            skSolve(sketch);
        }
        {
            var Q0;
            Q0 = qSketchRegion(id + "F44", true);
            extrude(context, id + "F45", {"entities" : qUnion([Q0]), "depth" : 3 * mm});
        }
        {
            var Q0;
            Q0=makeQuery(id+"F45.opExtrude","CAP_FACE",FACE,{"disambiguationData":[OSD([sQuery(id+"F44.wireOp",EDGE,"E76.0"),sQuery(id+"F44.wireOp",EDGE,"E76.1"),sQuery(id+"F44.wireOp",EDGE,"E76.2"),sQuery(id+"F44.wireOp",EDGE,"E76.3"),sQuery(id+"F44.wireOp",EDGE,"E76.4"),sQuery(id+"F44.wireOp",EDGE,"E76.5"),sQuery(id+"F44.wireOp",EDGE,"E76.6"),sQuery(id+"F44.wireOp",EDGE,"E76.7")])],"isStart":true});
            var sketch = newSketch(context, id + "F46", { "sketchPlane" : qUnion([Q0])});
            skLineSegment(sketch, "E77.0", {"start": v(17, -33) * mm, "end": v(-17, -33) * mm});
            skLineSegment(sketch, "E77.1", {"start": v(-17, 33) * mm, "end": v(-17, -33) * mm});
            skLineSegment(sketch, "E77.2", {"start": v(17, 33) * mm, "end": v(17, -33) * mm});
            skLineSegment(sketch, "E77.3", {"start": v(17, 33) * mm, "end": v(-17, 33) * mm});
            skSolve(sketch);
        }
        {
            var Q0;
            Q0 = qSketchRegion(id + "F46", true);
            extrude(context, id + "F47", {"entities" : qUnion([Q0]), "operationType" : NewBodyOperationType.ADD, "depth" : 2 * mm});
        }
        {
            var Q0;
            Q0=makeQuery(id+"F47.opExtrude","CAP_FACE",FACE,{"disambiguationData":[OSD([sQuery(id+"F46.wireOp",EDGE,"E77.0"),sQuery(id+"F46.wireOp",EDGE,"E77.1"),sQuery(id+"F46.wireOp",EDGE,"E77.2"),sQuery(id+"F46.wireOp",EDGE,"E77.3")])],"isStart":false});
            var sketch = newSketch(context, id + "F48", { "sketchPlane" : qUnion([Q0])});
            skCircle(sketch, "E78", {"center": v(-7.1, -29.25) * mm, "radius": 2.5 * mm});
            skCircle(sketch, "E79.0", {"center": v(13, 29) * mm, "radius": 1.5 * mm});
            skCircle(sketch, "E80", {"center": v(13, 29) * mm, "radius": 2.5 * mm});
            skCircle(sketch, "E81.0", {"center": v(-7.1, -29.25) * mm, "radius": 1.5 * mm});
            skSolve(sketch);
        }
        {
            var Q0;
            Q0 = qSketchRegion(id + "F48", true);
            extrude(context, id + "F49", {"entities" : qUnion([Q0]), "operationType" : NewBodyOperationType.ADD, "depth" : 10 * mm});
        }
    });
